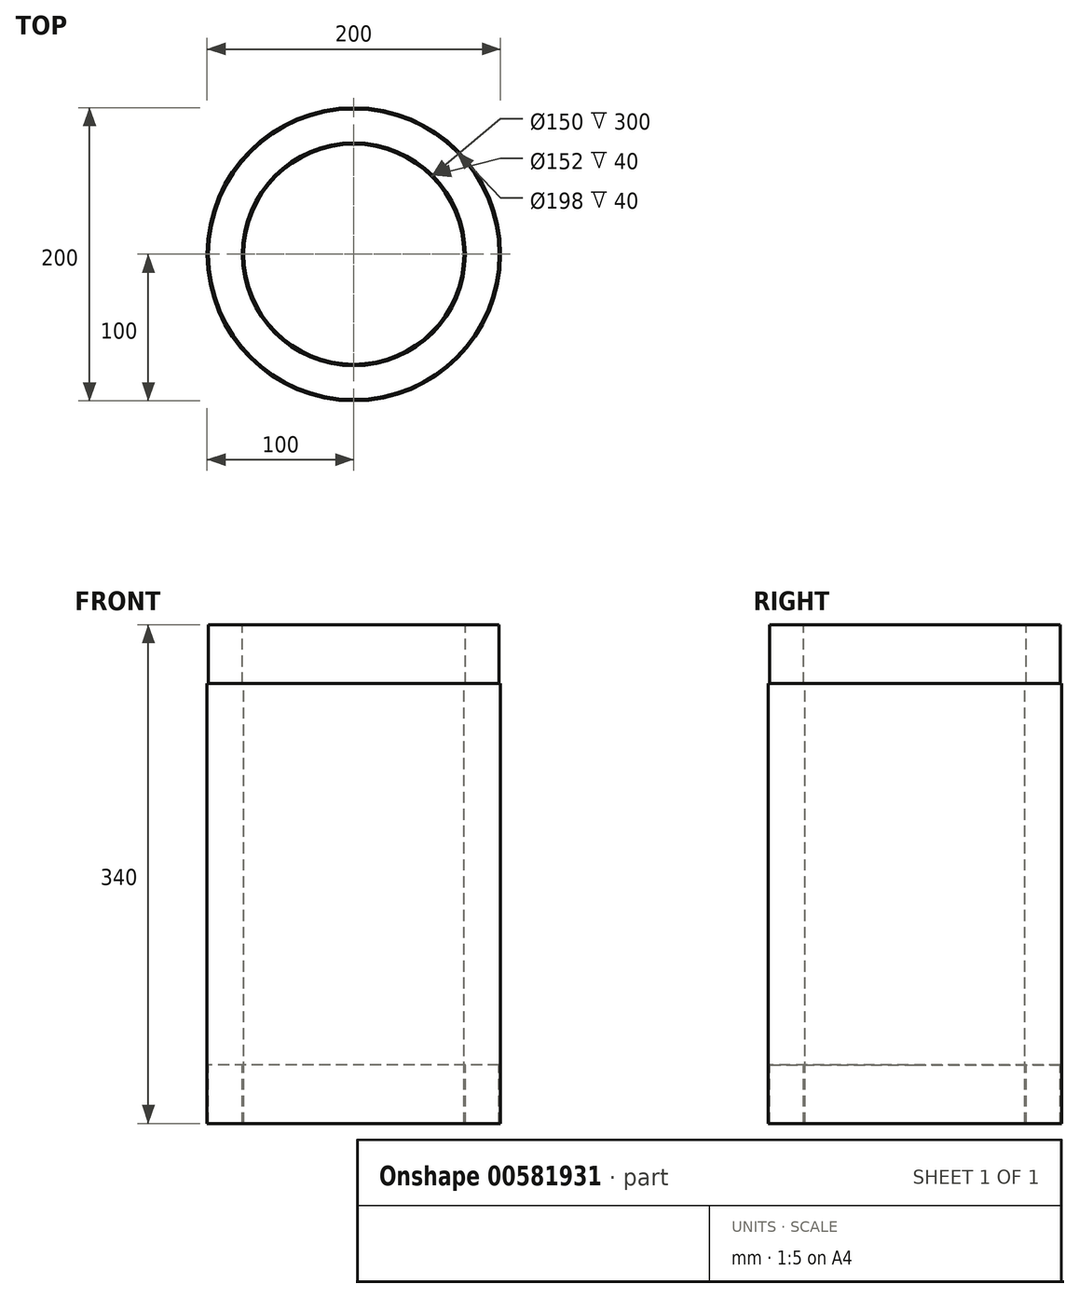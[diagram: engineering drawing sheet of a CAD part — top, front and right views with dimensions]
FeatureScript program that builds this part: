
annotation { "Feature Type Name" : "Feature", "Feature Type Description" : "" }
export const myFeature = defineFeature(function(context is Context, id is Id, definition is map)
    precondition{}
    {
        {
            var Q0;
            Q0=qCreatedBy(makeId("Front.planeOp"),FACE);
            var sketch = newSketch(context, id + "F0", { "sketchPlane" : qUnion([Q0])});
            skLineSegment(sketch, "E0", {"start": v(0, 345.75) * mm, "end": v(0, -558.03) * mm, "construction": true});
            skLineSegment(sketch, "E1", {"start": v(-75, -518.84) * mm, "end": v(-75, -218.84) * mm});
            skLineSegment(sketch, "E2", {"start": v(-75, -218.84) * mm, "end": v(-76, -218.84) * mm});
            skLineSegment(sketch, "E3", {"start": v(-76, -218.84) * mm, "end": v(-76, -178.84) * mm});
            skLineSegment(sketch, "E4", {"start": v(-76, -178.84) * mm, "end": v(-99, -178.84) * mm});
            skLineSegment(sketch, "E5", {"start": v(-99, -178.84) * mm, "end": v(-99, -218.84) * mm});
            skLineSegment(sketch, "E6", {"start": v(-99, -218.84) * mm, "end": v(-100, -218.84) * mm});
            skLineSegment(sketch, "E7", {"start": v(-100, -218.84) * mm, "end": v(-100, -518.84) * mm});
            skLineSegment(sketch, "E8", {"start": v(-100, -518.84) * mm, "end": v(-99, -518.84) * mm});
            skLineSegment(sketch, "E9", {"start": v(-99, -518.84) * mm, "end": v(-99, -478.84) * mm});
            skLineSegment(sketch, "E10", {"start": v(-99, -478.84) * mm, "end": v(-76, -478.84) * mm});
            skLineSegment(sketch, "E11", {"start": v(-76, -478.84) * mm, "end": v(-76, -518.84) * mm});
            skLineSegment(sketch, "E12", {"start": v(-76, -518.84) * mm, "end": v(-75, -518.84) * mm});
            skSolve(sketch);
        }
        {
            var Q0;
            Q0=qSketchRegion(id+"F0",true);
            var Q1;
            Q1=sQuery(id+"F0.wireOp",EDGE,"E0");
            revolve(context, id + "F1", {"entities" : qUnion([Q0]), "axis" : qUnion([Q1]), "revolveType" : RevolveType.FULL});
        }
    });
